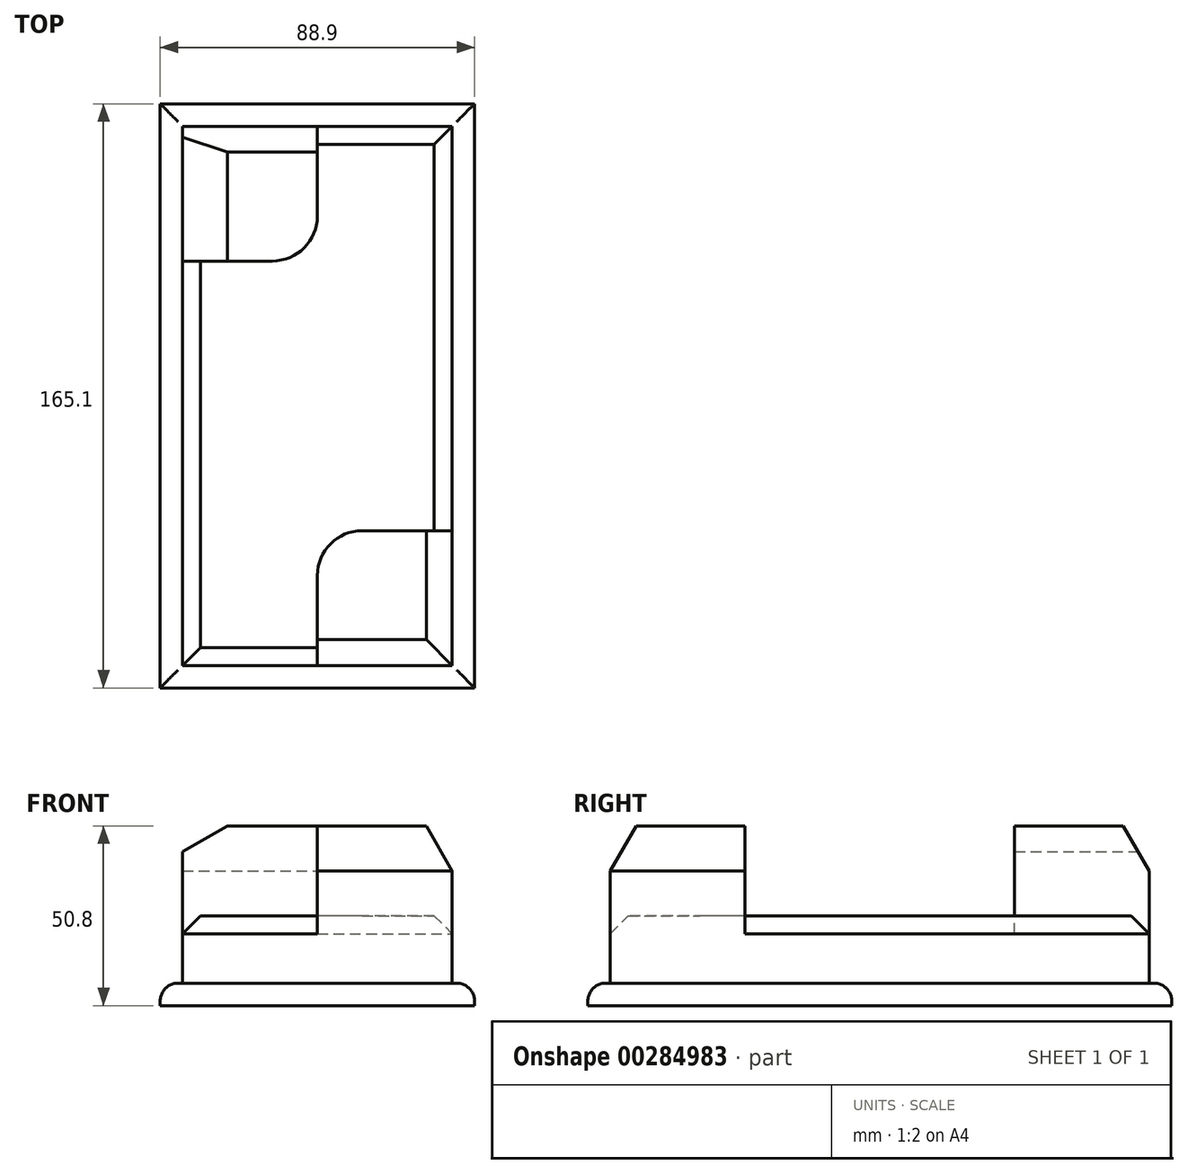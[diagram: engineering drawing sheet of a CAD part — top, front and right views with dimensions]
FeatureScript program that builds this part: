
annotation { "Feature Type Name" : "Feature", "Feature Type Description" : "" }
export const myFeature = defineFeature(function(context is Context, id is Id, definition is map)
    precondition{}
    {
        {
            var Q0;
            Q0=qCreatedBy(makeId("Top.planeOp"),FACE);
            var sketch = newSketch(context, id + "F0", { "sketchPlane" : qUnion([Q0])});
            skLineSegment(sketch, "E0.bottom", {"start": v(-38.1, 76.2) * mm, "end": v(38.1, 76.2) * mm});
            skLineSegment(sketch, "E0.top", {"start": v(-38.1, -76.2) * mm, "end": v(38.1, -76.2) * mm});
            skLineSegment(sketch, "E0.left", {"start": v(-38.1, 76.2) * mm, "end": v(-38.1, -76.2) * mm});
            skLineSegment(sketch, "E0.right", {"start": v(38.1, 76.2) * mm, "end": v(38.1, -76.2) * mm});
            skPoint(sketch, "E0.middle", {"position": v(0, 0) * mm});
            skLineSegment(sketch, "E1.0", {"start": v(-44.45, 82.55) * mm, "end": v(-44.45, -82.55) * mm});
            skLineSegment(sketch, "E1.1", {"start": v(-44.45, 82.55) * mm, "end": v(44.45, 82.55) * mm});
            skLineSegment(sketch, "E1.2", {"start": v(44.45, 82.55) * mm, "end": v(44.45, -82.55) * mm});
            skLineSegment(sketch, "E1.3", {"start": v(-44.45, -82.55) * mm, "end": v(44.45, -82.55) * mm});
            skLineSegment(sketch, "E2", {"start": v(0, 76.2) * mm, "end": v(0, 50.8) * mm});
            skPoint(sketch, "E2.endSnap0", {"position": v(0, 76.2) * mm});
            skLineSegment(sketch, "E3", {"start": v(-12.7, 38.1) * mm, "end": v(-38.1, 38.1) * mm});
            skPoint(sketch, "E4.visualSharp", {"position": v(0, 38.1) * mm});
            skArc(sketch, "E4.filletArc", {"start": v(-12.7, 38.1) * mm, "mid": v(-3.72, 41.82) * mm, "end": v(0, 50.8) * mm});
            skLineSegment(sketch, "E5", {"start": v(0, -76.2) * mm, "end": v(0, -50.8) * mm});
            skPoint(sketch, "E5.endSnap0", {"position": v(0, -76.2) * mm});
            skLineSegment(sketch, "E6", {"start": v(12.7, -38.1) * mm, "end": v(38.1, -38.1) * mm});
            skPoint(sketch, "E7.visualSharp", {"position": v(0, -38.1) * mm});
            skArc(sketch, "E7.filletArc", {"start": v(12.7, -38.1) * mm, "mid": v(3.72, -41.82) * mm, "end": v(0, -50.8) * mm});
            skSolve(sketch);
        }
        {
            var Q0;
            Q0=makeQuery(id+"F0.imprint","IMPRINT",FACE,{"disambiguationData":[TD([[makeQuery(id+"F0.imprint","IMPRINT",EDGE,{"derivedFrom":sQuery(id+"F0.wireOp",EDGE,"E1.0")}),1.0]])]});
            extrude(context, id + "F1", {"entities" : qUnion([Q0]), "depth" : 6.35 * mm});
        }
        {
            var Q0;
            {var subQ9=sQuery(id+"F0.wireOp",EDGE,"E2");Q0=makeQuery(id+"F0.imprint","IMPRINT",FACE,{"disambiguationData":[TD([[makeQuery(id+"F0.imprint","IMPRINT",EDGE,{"derivedFrom":subQ9}),1.0]])]});}
            extrude(context, id + "F2", {"entities" : qUnion([Q0]), "operationType" : NewBodyOperationType.ADD, "depth" : 25.4 * mm});
        }
        {
            var Q0;
            Q0=makeQuery(id+"F2.opExtrude","CAP_EDGE",EDGE,{"disambiguationData":[OSD([sQuery(id+"F0.wireOp",EDGE,"E0.left")])],"isStart":false});
            var Q1;
            Q1=makeQuery(id+"F2.opExtrude","CAP_EDGE",EDGE,{"disambiguationData":[OSD([sQuery(id+"F0.wireOp",EDGE,"E0.top")])],"isStart":false});
            var Q2;
            Q2=makeQuery(id+"F2.opExtrude","CAP_EDGE",EDGE,{"disambiguationData":[OSD([sQuery(id+"F0.wireOp",EDGE,"E0.right")])],"isStart":false});
            var Q3;
            Q3=makeQuery(id+"F2.opExtrude","CAP_EDGE",EDGE,{"disambiguationData":[OSD([sQuery(id+"F0.wireOp",EDGE,"E0.bottom")])],"isStart":false});
            chamfer(context, id + "F3", {"entities" : qUnion([Q0, Q1, Q2, Q3]), "width" : 5.08 * mm, "tangentPropagation" : true});
        }
        {
            var Q0;
            {var subQ1=sQuery(id+"F0.wireOp",EDGE,"E5");Q0=makeQuery(id+"F0.imprint","IMPRINT",FACE,{"disambiguationData":[TD([[makeQuery(id+"F0.imprint","IMPRINT",EDGE,{"derivedFrom":subQ1}),-1.0]])]});}
            var Q1;
            {var subQ1=sQuery(id+"F0.wireOp",EDGE,"E2");Q1=makeQuery(id+"F0.imprint","IMPRINT",FACE,{"disambiguationData":[TD([[makeQuery(id+"F0.imprint","IMPRINT",EDGE,{"derivedFrom":subQ1}),-1.0]])]});}
            extrude(context, id + "F4", {"entities" : qUnion([Q0, Q1]), "operationType" : NewBodyOperationType.ADD, "depth" : 50.8 * mm});
        }
        {
            var Q0;
            Q0=makeQuery(id+"F1.opExtrude","CAP_EDGE",EDGE,{"disambiguationData":[OSD([sQuery(id+"F0.wireOp",EDGE,"E1.1")])],"isStart":false});
            var Q1;
            Q1=makeQuery(id+"F1.opExtrude","CAP_EDGE",EDGE,{"disambiguationData":[OSD([sQuery(id+"F0.wireOp",EDGE,"E1.0")])],"isStart":false});
            var Q2;
            Q2=makeQuery(id+"F1.opExtrude","CAP_EDGE",EDGE,{"disambiguationData":[OSD([sQuery(id+"F0.wireOp",EDGE,"E1.3")])],"isStart":false});
            var Q3;
            Q3=makeQuery(id+"F1.opExtrude","CAP_EDGE",EDGE,{"disambiguationData":[OSD([sQuery(id+"F0.wireOp",EDGE,"E1.2")])],"isStart":false});
            fillet(context, id + "F5", {"entities" : qUnion([Q0, Q1, Q2, Q3]), "radius" : 5.08 * mm, "tangentPropagation" : true, "allowEdgeOverflow" : false});
        }
        {
            var Q0;
            Q0=makeQuery(id+"F4.opExtrude","CAP_EDGE",EDGE,{"disambiguationData":[OSD([sQuery(id+"F0.wireOp",EDGE,"E0.right")])],"isStart":false});
            var Q1;
            Q1=makeQuery(id+"F4.opExtrude","CAP_EDGE",EDGE,{"disambiguationData":[OSD([sQuery(id+"F0.wireOp",EDGE,"E0.top")])],"isStart":false});
            var Q2;
            Q2=makeQuery(id+"F4.opExtrude","CAP_EDGE",EDGE,{"disambiguationData":[OSD([sQuery(id+"F0.wireOp",EDGE,"E0.bottom")])],"isStart":false});
            var Q3;
            Q3=makeQuery(id+"F4.opExtrude","CAP_EDGE",EDGE,{"disambiguationData":[OSD([sQuery(id+"F0.wireOp",EDGE,"E0.left")])],"isStart":false});
            chamfer(context, id + "F6", {"entities" : qUnion([Q0, Q1, Q2, Q3]), "chamferType" : ChamferType.OFFSET_ANGLE, "width" : 12.7 * mm, "oppositeDirection" : false, "angle" : 30 * degree});
        }
    });
